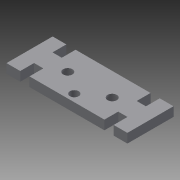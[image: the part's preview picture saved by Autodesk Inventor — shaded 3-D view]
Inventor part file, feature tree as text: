
AUTODESK INVENTOR PART (.ipt)
format: ipt  version: 2015 (Build 190159000, 159)  size: 118,272 bytes
history: native  units: mm
features: sketch x3, extrude x3, plane x1
ambient origin geometry x8: Origin, YZ Plane, XZ Plane, XY Plane, X Axis, Y Axis, Z Axis, Center Point
bodies: Body1 (feature_tree)
feature tree (7):
  sketch  "Sketch1"  dims[d0=15.0mm d1=15.0mm d2=15.0mm d3=15.0mm d8=15.0mm]
  plane  "Work Plane1"
  sketch  "Sketch2"  dims[d9=15.0mm d20=2.5mm]
  extrude  "Extrusion11"  Depth=15.0mm
  extrude  "Extrusion12"  Depth=15.0mm
  extrude  "Extrusion14"  Depth=10.0mm
  sketch  "Sketch4"  dims[d23=8.0mm d24=9.5mm d27=10.0mm d28=10.0mm d39=10.0mm d40=0.0mm d41=8.0mm d42=0.0mm d50=5.0mm d51=2.5mm d52=10.0mm d53=0.0mm]
